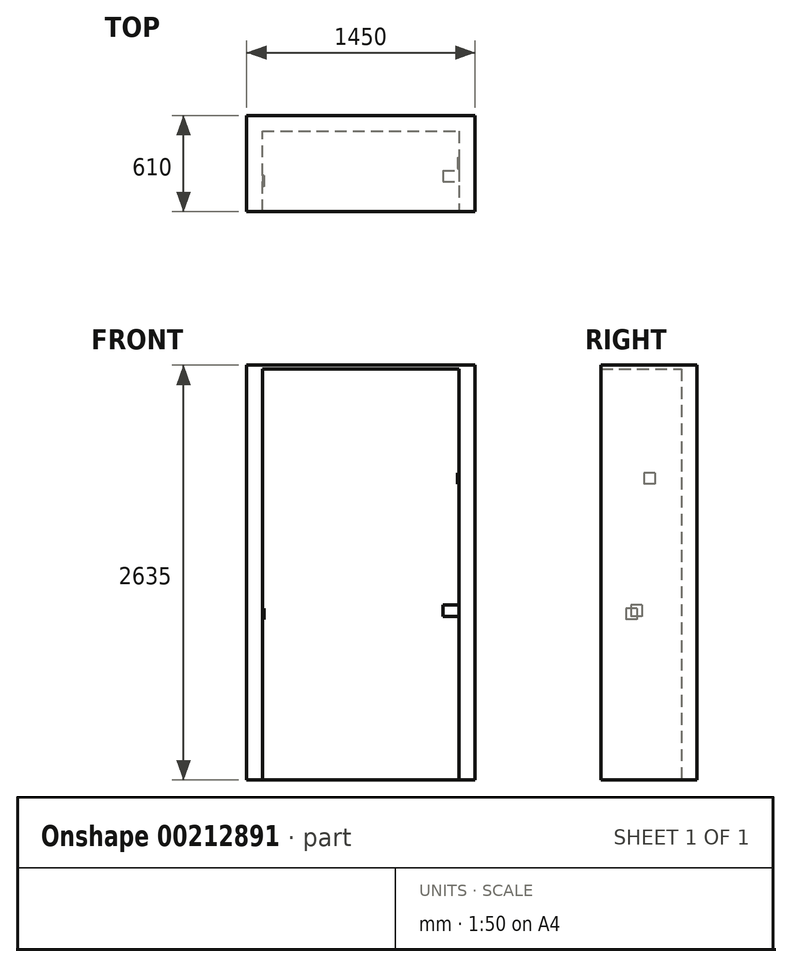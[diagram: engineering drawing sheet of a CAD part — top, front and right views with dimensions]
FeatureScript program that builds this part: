
annotation { "Feature Type Name" : "Feature", "Feature Type Description" : "" }
export const myFeature = defineFeature(function(context is Context, id is Id, definition is map)
    precondition{}
    {
        {
            var Q0;
            Q0=qCreatedBy(makeId("Top.planeOp"),FACE);
            var sketch = newSketch(context, id + "F0", { "sketchPlane" : qUnion([Q0])});
            skLineSegment(sketch, "E0", {"start": v(0, -510) * mm, "end": v(0, 0) * mm});
            skLineSegment(sketch, "E1", {"start": v(0, 0) * mm, "end": v(1250, 0) * mm});
            skLineSegment(sketch, "E2", {"start": v(1250, 0) * mm, "end": v(1250, -510) * mm});
            skLineSegment(sketch, "E3", {"start": v(1250, -510) * mm, "end": v(1350, -510) * mm});
            skLineSegment(sketch, "E4", {"start": v(1350, -510) * mm, "end": v(1350, 100) * mm});
            skLineSegment(sketch, "E5", {"start": v(1350, 100) * mm, "end": v(-100, 100) * mm});
            skLineSegment(sketch, "E6", {"start": v(-100, 100) * mm, "end": v(-100, -510) * mm});
            skLineSegment(sketch, "E7", {"start": v(-100, -510) * mm, "end": v(0, -510) * mm});
            skSolve(sketch);
        }
        {
            var Q0;
            Q0=makeQuery(id+"F0.imprint","IMPRINT",FACE,{"disambiguationData":[TD([[makeQuery(id+"F0.imprint","IMPRINT",EDGE,{"derivedFrom":sQuery(id+"F0.wireOp",EDGE,"E0")}),1.0]])]});
            extrude(context, id + "F1", {"entities" : qUnion([Q0]), "depth" : 2610 * mm});
        }
        {
            var Q0;
            Q0=makeQuery(id+"F1.opExtrude","CAP_FACE",FACE,{"disambiguationData":[OSD([sQuery(id+"F0.wireOp",EDGE,"E0"),sQuery(id+"F0.wireOp",EDGE,"E1"),sQuery(id+"F0.wireOp",EDGE,"E2"),sQuery(id+"F0.wireOp",EDGE,"E3"),sQuery(id+"F0.wireOp",EDGE,"E4"),sQuery(id+"F0.wireOp",EDGE,"E5"),sQuery(id+"F0.wireOp",EDGE,"E6"),sQuery(id+"F0.wireOp",EDGE,"E7")])],"isStart":false});
            var sketch = newSketch(context, id + "F2", { "sketchPlane" : qUnion([Q0])});
            skLineSegment(sketch, "E8.bottom", {"start": v(-100, 100) * mm, "end": v(1350, 100) * mm});
            skLineSegment(sketch, "E8.top", {"start": v(-100, -510) * mm, "end": v(1350, -510) * mm});
            skLineSegment(sketch, "E8.left", {"start": v(-100, 100) * mm, "end": v(-100, -510) * mm});
            skLineSegment(sketch, "E8.right", {"start": v(1350, 100) * mm, "end": v(1350, -510) * mm});
            skSolve(sketch);
        }
        {
            var Q0;
            Q0 = qSketchRegion(id + "F2", true);
            extrude(context, id + "F3", {"entities" : qUnion([Q0]), "operationType" : NewBodyOperationType.ADD, "depth" : 25 * mm});
        }
        {
            var Q0;
            Q0=makeQuery(id+"F1.opExtrude","SWEPT_FACE",FACE,{"disambiguationData":[OSD([sQuery(id+"F0.wireOp",EDGE,"E1")])]});
            var sketch = newSketch(context, id + "F4", { "sketchPlane" : qUnion([Q0])});
            skCircle(sketch, "E9", {"center": v(1177.5, 2312.5) * mm, "radius": 72.5 * mm});
            skSolve(sketch);
        }
        {
            var Q0;
            Q0=makeQuery(id+"F1.opExtrude","SWEPT_FACE",FACE,{"disambiguationData":[OSD([sQuery(id+"F0.wireOp",EDGE,"E2")])]});
            var sketch = newSketch(context, id + "F5", { "sketchPlane" : qUnion([Q0])});
            skLineSegment(sketch, "E10.bottom", {"start": v(250, 1110) * mm, "end": v(320, 1110) * mm});
            skLineSegment(sketch, "E10.top", {"start": v(250, 1040) * mm, "end": v(320, 1040) * mm});
            skLineSegment(sketch, "E10.left", {"start": v(250, 1110) * mm, "end": v(250, 1040) * mm});
            skLineSegment(sketch, "E10.right", {"start": v(320, 1110) * mm, "end": v(320, 1040) * mm});
            skLineSegment(sketch, "E11.bottom", {"start": v(168.02, 1950.46) * mm, "end": v(238.02, 1950.46) * mm});
            skLineSegment(sketch, "E11.top", {"start": v(168.02, 1880.46) * mm, "end": v(238.02, 1880.46) * mm});
            skLineSegment(sketch, "E11.left", {"start": v(168.02, 1950.46) * mm, "end": v(168.02, 1880.46) * mm});
            skLineSegment(sketch, "E11.right", {"start": v(238.02, 1950.46) * mm, "end": v(238.02, 1880.46) * mm});
            skSolve(sketch);
        }
        {
            var Q0;
            Q0=makeQuery(id+"F5.imprint","IMPRINT",FACE,{"disambiguationData":[TD([[makeQuery(id+"F5.imprint","IMPRINT",EDGE,{"derivedFrom":sQuery(id+"F5.wireOp",EDGE,"E10.bottom")}),-1.0]])]});
            extrude(context, id + "F6", {"entities" : qUnion([Q0]), "operationType" : NewBodyOperationType.ADD, "depth" : 104 * mm});
        }
        {
            var Q0;
            Q0=makeQuery(id+"F5.imprint","IMPRINT",FACE,{"disambiguationData":[TD([[makeQuery(id+"F5.imprint","IMPRINT",EDGE,{"derivedFrom":sQuery(id+"F5.wireOp",EDGE,"E11.bottom")}),-1.0]])]});
            extrude(context, id + "F7", {"entities" : qUnion([Q0]), "operationType" : NewBodyOperationType.ADD, "depth" : 10 * mm});
        }
        {
            var Q0;
            Q0=makeQuery(id+"F1.opExtrude","SWEPT_FACE",FACE,{"disambiguationData":[OSD([sQuery(id+"F0.wireOp",EDGE,"E0")])]});
            var sketch = newSketch(context, id + "F8", { "sketchPlane" : qUnion([Q0])});
            skLineSegment(sketch, "E12.bottom", {"start": v(-279.72, 1090) * mm, "end": v(-349.72, 1090) * mm});
            skLineSegment(sketch, "E12.top", {"start": v(-279.72, 1020) * mm, "end": v(-349.72, 1020) * mm});
            skLineSegment(sketch, "E12.left", {"start": v(-279.72, 1090) * mm, "end": v(-279.72, 1020) * mm});
            skLineSegment(sketch, "E12.right", {"start": v(-349.72, 1090) * mm, "end": v(-349.72, 1020) * mm});
            skSolve(sketch);
        }
        {
            var Q0;
            Q0=makeQuery(id+"F8.imprint","IMPRINT",FACE,{"disambiguationData":[TD([[makeQuery(id+"F8.imprint","IMPRINT",EDGE,{"derivedFrom":sQuery(id+"F8.wireOp",EDGE,"E12.bottom")}),1.0]])]});
            extrude(context, id + "F9", {"entities" : qUnion([Q0]), "operationType" : NewBodyOperationType.ADD, "depth" : 10 * mm});
        }
        {
            var Q0;
            Q0=sQuery(id+"F4.wireOp",EDGE,"E9");
            extrude(context, id + "F10", {"bodyType" : ToolBodyType.SURFACE, "surfaceEntities" : qUnion([Q0]), "depth" : 510 * mm});
        }
    });
